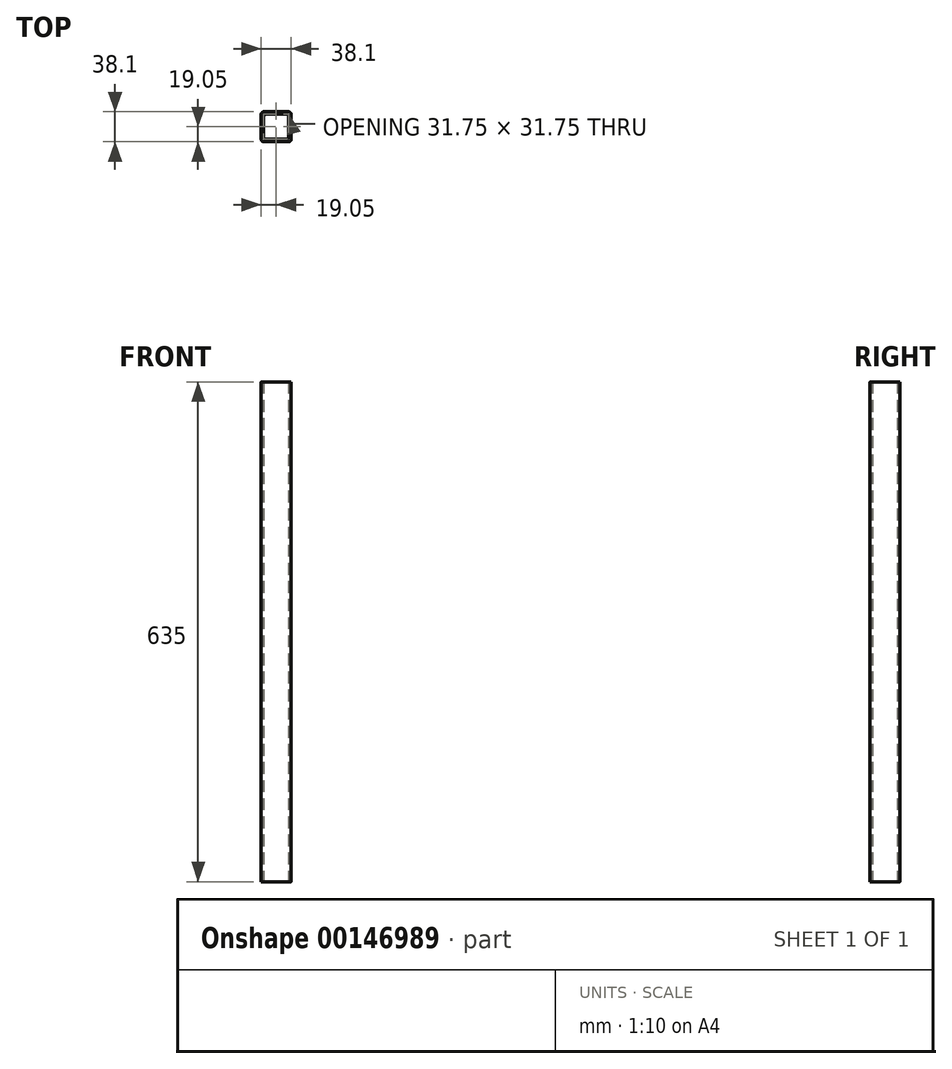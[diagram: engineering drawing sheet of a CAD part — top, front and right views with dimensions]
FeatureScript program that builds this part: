
annotation { "Feature Type Name" : "Feature", "Feature Type Description" : "" }
export const myFeature = defineFeature(function(context is Context, id is Id, definition is map)
    precondition{}
    {
        {
            var Q0;
            Q0=qCreatedBy(makeId("Top.planeOp"),FACE);
            var sketch = newSketch(context, id + "F0", { "sketchPlane" : qUnion([Q0])});
            skLineSegment(sketch, "E0.bottom", {"start": v(15.87, 19.05) * mm, "end": v(-15.88, 19.05) * mm});
            skLineSegment(sketch, "E0.top", {"start": v(15.88, -19.05) * mm, "end": v(-15.87, -19.05) * mm});
            skLineSegment(sketch, "E0.left", {"start": v(19.05, 15.88) * mm, "end": v(19.05, -15.88) * mm});
            skLineSegment(sketch, "E0.right", {"start": v(-19.05, 15.87) * mm, "end": v(-19.05, -15.88) * mm});
            skPoint(sketch, "E0.middle", {"position": v(0, 0) * mm});
            skPoint(sketch, "E1.visualSharp", {"position": v(-19.05, 19.05) * mm});
            skArc(sketch, "E1.filletArc", {"start": v(-15.88, 19.05) * mm, "mid": v(-18.12, 18.12) * mm, "end": v(-19.05, 15.87) * mm});
            skPoint(sketch, "E2.visualSharp", {"position": v(19.05, 19.05) * mm});
            skArc(sketch, "E2.filletArc", {"start": v(19.05, 15.88) * mm, "mid": v(18.12, 18.12) * mm, "end": v(15.87, 19.05) * mm});
            skPoint(sketch, "E3.visualSharp", {"position": v(-19.05, -19.05) * mm});
            skArc(sketch, "E3.filletArc", {"start": v(-19.05, -15.88) * mm, "mid": v(-18.12, -18.12) * mm, "end": v(-15.87, -19.05) * mm});
            skPoint(sketch, "E4.visualSharp", {"position": v(19.05, -19.05) * mm});
            skArc(sketch, "E4.filletArc", {"start": v(15.88, -19.05) * mm, "mid": v(18.12, -18.12) * mm, "end": v(19.05, -15.88) * mm});
            skLineSegment(sketch, "E5.bottom", {"start": v(12.7, 15.88) * mm, "end": v(-12.7, 15.88) * mm});
            skLineSegment(sketch, "E5.top", {"start": v(12.7, -15.88) * mm, "end": v(-12.7, -15.88) * mm});
            skLineSegment(sketch, "E5.left", {"start": v(15.87, 12.7) * mm, "end": v(15.88, -12.7) * mm});
            skLineSegment(sketch, "E5.right", {"start": v(-15.88, 12.7) * mm, "end": v(-15.87, -12.7) * mm});
            skArc(sketch, "E6.filletArc", {"start": v(-12.7, 15.88) * mm, "mid": v(-14.95, 14.95) * mm, "end": v(-15.88, 12.7) * mm});
            skArc(sketch, "E7.filletArc", {"start": v(15.88, 12.7) * mm, "mid": v(14.95, 14.95) * mm, "end": v(12.7, 15.88) * mm});
            skArc(sketch, "E8.filletArc", {"start": v(-15.88, -12.7) * mm, "mid": v(-14.95, -14.95) * mm, "end": v(-12.7, -15.88) * mm});
            skPoint(sketch, "E9.visualSharp", {"position": v(15.88, -15.87) * mm});
            skArc(sketch, "E9.filletArc", {"start": v(12.7, -15.88) * mm, "mid": v(14.95, -14.95) * mm, "end": v(15.88, -12.7) * mm});
            skSolve(sketch);
        }
        {
            var Q0;
            Q0 = qSketchRegion(id + "F0", true);
            extrude(context, id + "F1", {"entities" : qUnion([Q0]), "depth" : 635 * mm});
        }
    });
